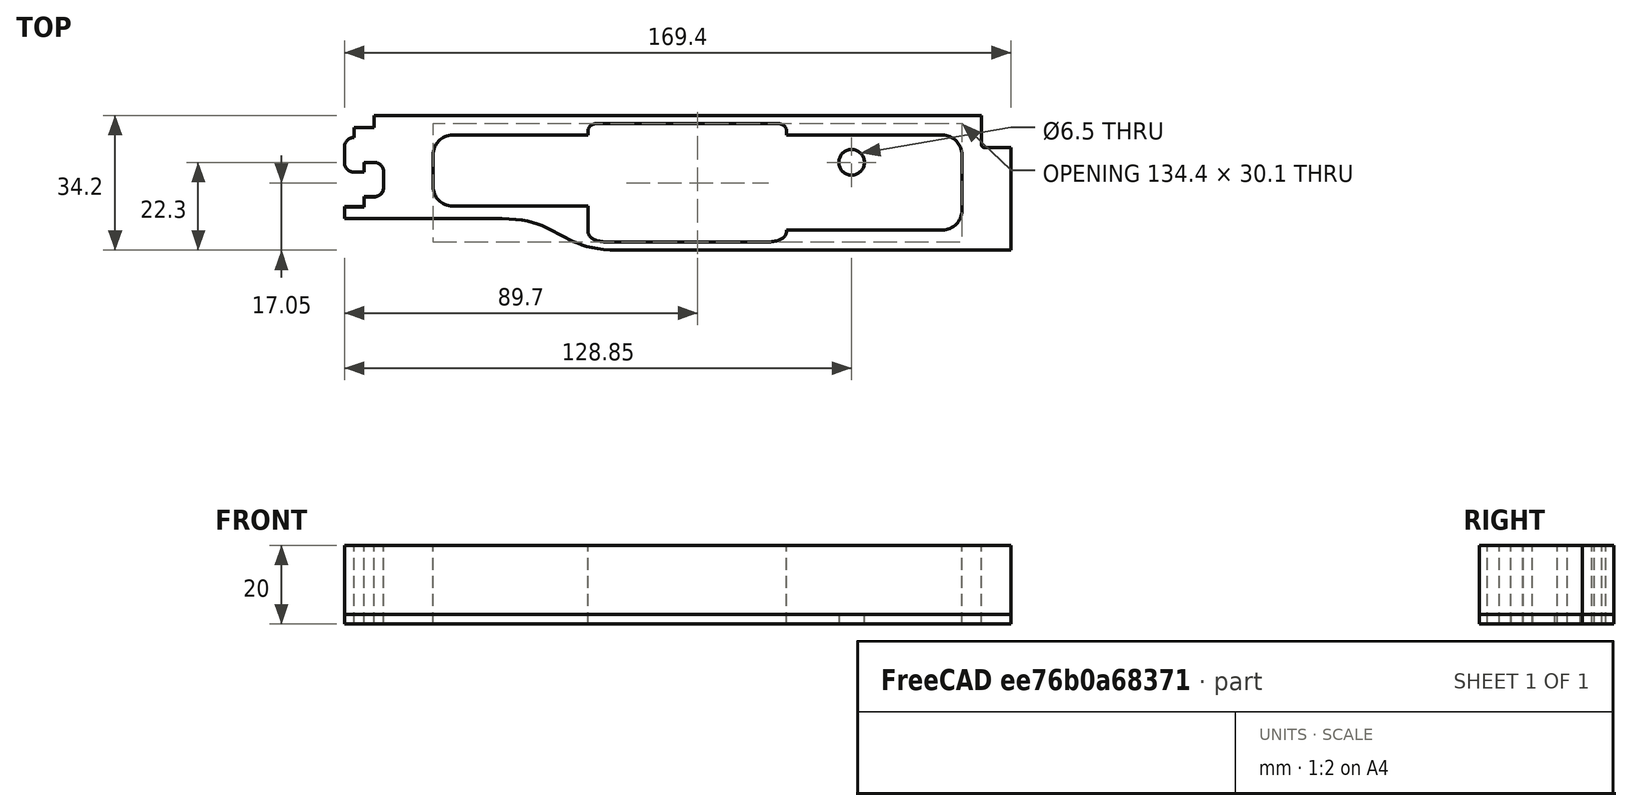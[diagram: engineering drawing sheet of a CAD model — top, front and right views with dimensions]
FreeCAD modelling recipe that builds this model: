
FCSTD DOCUMENT  (FreeCAD 0.19R0.19.2)
Label: v0_28
License: All rights reserved
LicenseURL: http://en.wikipedia.org/wiki/All_rights_reserved
objects: Sketcher::SketchObject×2, Part::Extrusion×2
note: 4 computed .brp shape members not serialized (recipe doc carries the construction recipe); baked Part::Feature solids carry a one-line shape summary decoded from their .brp

FEATURE [Sketcher::SketchObject] Sketch
  FullyConstrained = true
  sketch-geometry (33):
    g0: LineSegment StartX=0 StartY=0 StartZ=0 EndX=154.4 EndY=0 EndZ=0
    g1: Circle CenterX=121.35 CenterY=-11.9 CenterZ=0 NormalX=0 NormalY=0 NormalZ=1 AngleXU=0 Radius=3.25
    g2: LineSegment StartX=154.4 StartY=0 StartZ=0 EndX=154.4 EndY=-7.6 EndZ=0
    g3: ArcOfCircle CenterX=154.9 CenterY=-7.6 CenterZ=0 NormalX=0 NormalY=0 NormalZ=1 AngleXU=0 Radius=0.5 StartAngle=3.14159 EndAngle=4.71239
    g4: LineSegment StartX=-5 StartY=-3.1 StartZ=0 EndX=0 EndY=-3.1 EndZ=0
    g5: LineSegment StartX=-5 StartY=-3.1 StartZ=0 EndX=-5 EndY=-5.6 EndZ=0
    g6: LineSegment StartX=-7.5 StartY=-8.1 StartZ=0 EndX=-7.5 EndY=-11.85 EndZ=0
    g7: ArcOfCircle CenterX=-5 CenterY=-8.1 CenterZ=0 NormalX=0 NormalY=0 NormalZ=1 AngleXU=0 Radius=2.5 StartAngle=1.5708 EndAngle=3.14159
    g8: LineSegment StartX=-5 StartY=-14.35 StartZ=0 EndX=-2.5 EndY=-14.35 EndZ=0
    g9: ArcOfCircle CenterX=-5 CenterY=-11.85 CenterZ=0 NormalX=0 NormalY=0 NormalZ=1 AngleXU=0 Radius=2.5 StartAngle=3.14159 EndAngle=4.71239
    g10: LineSegment StartX=-2.5 StartY=-14.35 StartZ=0 EndX=-2.5 EndY=-11.85 EndZ=0
    g11: LineSegment StartX=-2.5 StartY=-11.85 StartZ=0 EndX=1.492e-13 EndY=-11.85 EndZ=0
    g12: ArcOfCircle CenterX=1.492e-13 CenterY=-14.35 CenterZ=0 NormalX=0 NormalY=0 NormalZ=1 AngleXU=0 Radius=2.5 StartAngle=8e-16 EndAngle=1.5708
    g13: LineSegment StartX=2.5 StartY=-14.35 StartZ=0 EndX=2.5 EndY=-18.1 EndZ=0
    g14: ArcOfCircle CenterX=1.474e-13 CenterY=-18.1 CenterZ=0 NormalX=0 NormalY=0 NormalZ=1 AngleXU=0 Radius=2.5 StartAngle=4.71239 EndAngle=6.28319
    g15: LineSegment StartX=-2.5 StartY=-20.6 StartZ=0 EndX=1.47e-13 EndY=-20.6 EndZ=0
    g16: LineSegment StartX=-2.5 StartY=-20.6 StartZ=0 EndX=-2.5 EndY=-23.1 EndZ=0
    g17: LineSegment StartX=-7.5 StartY=-23.1 StartZ=0 EndX=-2.5 EndY=-23.1 EndZ=0
    g18: LineSegment StartX=32.5209 StartY=-26.2 StartZ=0 EndX=-7.5 EndY=-26.2 EndZ=0
    g19: LineSegment StartX=61.85 StartY=-34.2 StartZ=0 EndX=161.9 EndY=-34.2 EndZ=0
    g20: LineSegment StartX=161.9 StartY=-8.1 StartZ=0 EndX=161.9 EndY=-34.2 EndZ=0
    g21: LineSegment StartX=154.9 StartY=-8.1 StartZ=0 EndX=161.9 EndY=-8.1 EndZ=0
    g22: LineSegment StartX=-7.5 StartY=-23.1 StartZ=0 EndX=-7.5 EndY=-26.2 EndZ=0
    g23: LineSegment StartX=0 StartY=0 StartZ=0 EndX=0 EndY=-3.1 EndZ=0
    g24-g28: Circle x5 (B-spline internal-alignment scaffolding for g29; pole/knot coordinates omitted)
    g29: BSplineCurve PolesCount=5 KnotsCount=3 Degree=3 IsPeriodic=0
    g30: GeomPoint X=61.85 Y=-34.2 Z=0
    g31: GeomPoint X=47.185 Y=-30.2 Z=0
    g32: GeomPoint X=32.5209 Y=-26.2 Z=0
  constraints (67):
    c: PointOnObject(g0,g-2)
    c: Horizontal(g0)
    c: Distance(g0) = 154.4
    c: DistanceY(g-1,g0) = 0
    c: Block(g1)
    c: Vertical(g2)
    c: Distance(g2) = 7.6
    c: Coincident(g2,g0)
    c: Block(g3)
    c: Horizontal(g4)
    c: Vertical(g5)
    c: Coincident(g5,g4)
    c: Vertical(g6)
    c: Coincident(g7,g5)
    c: Block(g7)
    c: Coincident(g6,g7)
    c: Horizontal(g8)
    c: Coincident(g9,g6)
    c: Block(g9)
    c: Block(g8)
    c: Vertical(g10)
    c: Coincident(g10,g8)
    c: Horizontal(g11)
    c: Coincident(g11,g10)
    c: Coincident(g12,g11)
    c: Vertical(g13)
    c: Block(g12)
    c: Coincident(g13,g12)
    c: Coincident(g14,g13)
    c: Block(g14)
    c: Horizontal(g15)
    c: Coincident(g15,g14)
    c: Vertical(g16)
    c: Coincident(g16,g15)
    c: Horizontal(g17)
    c: Coincident(g17,g16)
    c: Block(g16)
    c: Block(g4)
    c: Horizontal(g19)
    c: Horizontal(g18)
    c: Block(g18)
    c: Block(g19)
    c: Vertical(g20)
    c: Distance(g20) = 26.1
    c: Coincident(g20,g19)
    c: Horizontal(g21)
    c: Coincident(g21,g20)
    c: Coincident(g21,g3)
    c: Distance(g21) = 7
    c: Distance(g16) = 2.5
    c: Distance(g16) = 2.5
    c: Block(g17)
    c: Vertical(g22)
    c: Coincident(g22,g17)
    c: Coincident(g22,g18)
    c: Vertical(g23)
    c: Coincident(g23,g0)
    c: Coincident(g23,g4)
    c: Coincident(g29,g19)
    c: Weight(g24) = 1
    c: Equal(g24, g25-g28) x4
    c: Coincident(g29,g18)
    c: InternalAlignment(g24-g28 -> g29) x5
    c: InternalAlignment(g30,g29)
    c: InternalAlignment(g31,g29)
    c: InternalAlignment(g32,g29)
    c: Block(g29)
FEATURE [Part::Extrusion] Extrude
  Base = -> Sketch
  Dir = (0,0,1)
  DirMode = 2
  FaceMakerClass = Part::FaceMakerBullseye
  LengthFwd = 2.4
  LengthRev = 0
  Solid = true
  Symmetric = false
FEATURE [Sketcher::SketchObject] Sketch001
  FullyConstrained = true
  sketch-geometry (61):
    g0: ArcOfCircle CenterX=144.4 CenterY=-10 CenterZ=0 NormalX=0 NormalY=0 NormalZ=1 AngleXU=0 Radius=5 StartAngle=0 EndAngle=1.5708
    g1: ArcOfCircle CenterX=20 CenterY=-18 CenterZ=0 NormalX=0 NormalY=0 NormalZ=1 AngleXU=0 Radius=5 StartAngle=3.14159 EndAngle=4.71239
    g2: ArcOfCircle CenterX=20 CenterY=-10 CenterZ=0 NormalX=0 NormalY=0 NormalZ=1 AngleXU=0 Radius=5 StartAngle=1.5708 EndAngle=3.14159
    g3: LineSegment StartX=32.5209 StartY=-26.2 StartZ=0 EndX=-7.49911 EndY=-26.2 EndZ=0
    g4: LineSegment StartX=61.85 StartY=-34.2 StartZ=0 EndX=161.9 EndY=-34.2 EndZ=0
    g5: ArcOfCircle CenterX=144.4 CenterY=-24.1 CenterZ=0 NormalX=0 NormalY=0 NormalZ=1 AngleXU=0 Radius=5 StartAngle=4.71239 EndAngle=6.28319
    g6: Circle CenterX=104.85 CenterY=-29.2 CenterZ=0 NormalX=0 NormalY=0 NormalZ=1 AngleXU=0 Radius=1
    g7: Circle CenterX=104.85 CenterY=-32.2 CenterZ=0 NormalX=0 NormalY=0 NormalZ=1 AngleXU=0 Radius=1
    g8: Circle CenterX=98.85 CenterY=-32.2 CenterZ=0 NormalX=0 NormalY=0 NormalZ=1 AngleXU=0 Radius=1
    g9: BSplineCurve PolesCount=3 KnotsCount=2 Degree=2 IsPeriodic=0
    g10: GeomPoint X=104.85 Y=-29.2 Z=0
    g11: GeomPoint X=98.85 Y=-32.2 Z=0
    g12: Circle CenterX=54.35 CenterY=-29.2 CenterZ=0 NormalX=0 NormalY=0 NormalZ=1 AngleXU=0 Radius=1
    g13: Circle CenterX=60.35 CenterY=-32.2 CenterZ=0 NormalX=0 NormalY=0 NormalZ=1 AngleXU=0 Radius=1
    g14: BSplineCurve PolesCount=3 KnotsCount=2 Degree=2 IsPeriodic=0
    g15: GeomPoint X=54.35 Y=-29.2 Z=0
    g16: GeomPoint X=60.35 Y=-32.2 Z=0
    g17: ArcOfCircle CenterX=56.35 CenterY=-4.1 CenterZ=0 NormalX=0 NormalY=0 NormalZ=1 AngleXU=0 Radius=2 StartAngle=1.5708 EndAngle=3.14159
    g18: ArcOfCircle CenterX=102.85 CenterY=-4.1 CenterZ=0 NormalX=0 NormalY=0 NormalZ=1 AngleXU=0 Radius=2 StartAngle=1e-16 EndAngle=1.5708
    g19: LineSegment StartX=0 StartY=0 StartZ=0 EndX=154.4 EndY=0 EndZ=0
    g20: ArcOfCircle CenterX=154.9 CenterY=-7.6 CenterZ=0 NormalX=0 NormalY=0 NormalZ=1 AngleXU=0 Radius=0.5 StartAngle=3.14159 EndAngle=4.71239
    g21-g25: Circle x5 (B-spline internal-alignment scaffolding for g26; pole/knot coordinates omitted)
    g26: BSplineCurve PolesCount=5 KnotsCount=3 Degree=3 IsPeriodic=0
    g27: GeomPoint X=61.85 Y=-34.2 Z=0
    g28: GeomPoint X=47.1857 Y=-30.2 Z=0
    g29: GeomPoint X=32.5209 Y=-26.2 Z=0
    g30: LineSegment StartX=154.4 StartY=0 StartZ=0 EndX=154.4 EndY=-7.6 EndZ=0
    g31: LineSegment StartX=154.9 StartY=-8.1 StartZ=0 EndX=161.9 EndY=-8.1 EndZ=0
    g32: LineSegment StartX=161.9 StartY=-8.1 StartZ=0 EndX=161.9 EndY=-34.2 EndZ=0
    g33: LineSegment StartX=0 StartY=0 StartZ=0 EndX=0 EndY=-3.1 EndZ=0
    g34: LineSegment StartX=0 StartY=-3.1 StartZ=0 EndX=-5 EndY=-3.1 EndZ=0
    g35: LineSegment StartX=-5 StartY=-3.1 StartZ=0 EndX=-5 EndY=-5.6 EndZ=0
    g36: ArcOfCircle CenterX=-5 CenterY=-8.1 CenterZ=0 NormalX=0 NormalY=0 NormalZ=1 AngleXU=0 Radius=2.5 StartAngle=1.5708 EndAngle=3.14159
    g37: LineSegment StartX=-7.5 StartY=-8.1 StartZ=0 EndX=-7.5 EndY=-11.9 EndZ=0
    g38: ArcOfCircle CenterX=-5 CenterY=-11.9 CenterZ=0 NormalX=0 NormalY=0 NormalZ=1 AngleXU=0 Radius=2.5 StartAngle=3.14159 EndAngle=4.71239
    g39: LineSegment StartX=-5 StartY=-14.4 StartZ=0 EndX=-2.5 EndY=-14.4 EndZ=0
    g40: LineSegment StartX=-2.5 StartY=-14.4 StartZ=0 EndX=-2.5 EndY=-11.9 EndZ=0
    g41: LineSegment StartX=-2.5 StartY=-11.9 StartZ=0 EndX=2.833e-13 EndY=-11.9 EndZ=0
    g42: ArcOfCircle CenterX=2.833e-13 CenterY=-14.4 CenterZ=0 NormalX=0 NormalY=0 NormalZ=1 AngleXU=0 Radius=2.5 StartAngle=9e-16 EndAngle=1.5708
    g43: LineSegment StartX=2.5 StartY=-14.4 StartZ=0 EndX=2.5 EndY=-18.2 EndZ=0
    g44: ArcOfCircle CenterX=2.796e-13 CenterY=-18.2 CenterZ=0 NormalX=0 NormalY=0 NormalZ=1 AngleXU=0 Radius=2.5 StartAngle=4.71239 EndAngle=6.28319
    g45: LineSegment StartX=-2.5 StartY=-20.7 StartZ=0 EndX=8.16987e-07 EndY=-20.7 EndZ=0
    g46: LineSegment StartX=-2.5 StartY=-20.7 StartZ=0 EndX=-2.5 EndY=-23.2 EndZ=0
    g47: LineSegment StartX=-7.5 StartY=-23.2 StartZ=0 EndX=-2.5 EndY=-23.2 EndZ=0
    g48: LineSegment StartX=-7.5 StartY=-23.2 StartZ=0 EndX=-7.49911 EndY=-26.2 EndZ=0
    g49: LineSegment StartX=20 StartY=-5 StartZ=0 EndX=54.35 EndY=-5 EndZ=0
    g50: LineSegment StartX=54.35 StartY=-5 StartZ=0 EndX=54.35 EndY=-4.1 EndZ=0
    g51: LineSegment StartX=56.35 StartY=-2.1 StartZ=0 EndX=102.85 EndY=-2.1 EndZ=0
    g52: LineSegment StartX=104.85 StartY=-4.1 StartZ=0 EndX=104.85 EndY=-5 EndZ=0
    g53: LineSegment StartX=104.85 StartY=-5 StartZ=0 EndX=144.4 EndY=-5 EndZ=0
    g54: LineSegment StartX=149.4 StartY=-10 StartZ=0 EndX=149.4 EndY=-24.1 EndZ=0
    g55: LineSegment StartX=144.4 StartY=-29.1 StartZ=0 EndX=104.85 EndY=-29.1 EndZ=0
    g56: LineSegment StartX=104.85 StartY=-29.1 StartZ=0 EndX=104.85 EndY=-29.2 EndZ=0
    g57: LineSegment StartX=98.85 StartY=-32.2 StartZ=0 EndX=60.35 EndY=-32.2 EndZ=0
    g58: LineSegment StartX=54.35 StartY=-29.2 StartZ=0 EndX=54.35 EndY=-23 EndZ=0
    g59: LineSegment StartX=54.35 StartY=-23 StartZ=0 EndX=20 EndY=-23 EndZ=0
    g60: LineSegment StartX=15 StartY=-18 StartZ=0 EndX=15 EndY=-10 EndZ=0
  constraints (121):
    c: PointOnObject(g19,g-2)
    c: DistanceY(g-1,g19) = 0
    c: Block(g0)
    c: Block(g1)
    c: Block(g2)
    c: Horizontal(g4)
    c: Horizontal(g3)
    c: Block(g5)
    c: Distance(g3) = 40.02
    c: Weight(g6) = 1
    c: Equal(g6,g7)
    c: Equal(g6,g8)
    c: InternalAlignment(g6,g9)
    c: InternalAlignment(g7,g9)
    c: InternalAlignment(g8,g9)
    c: InternalAlignment(g10,g9)
    c: InternalAlignment(g11,g9)
    c: Block(g9)
    c: Weight(g12) = 1
    c: Equal(g12,g13)
    c: InternalAlignment(g12,g14)
    c: InternalAlignment(g13,g14)
    c: InternalAlignment(g15,g14)
    c: InternalAlignment(g16,g14)
    c: Block(g14)
    c: Block(g17)
    c: Block(g18)
    c: Horizontal(g19)
    c: Block(g4)
    c: Block(g19)
    c: Block(g20)
    c: Coincident(g26,g4)
    c: Weight(g21) = 1
    c: Equal(g21, g22-g25) x4
    c: Coincident(g26,g3)
    c: InternalAlignment(g21-g25 -> g26) x5
    c: InternalAlignment(g27,g26)
    c: InternalAlignment(g28,g26)
    c: InternalAlignment(g29,g26)
    c: Block(g26)
    c: Vertical(g30)
    c: Coincident(g30,g19)
    c: Coincident(g20,g30)
    c: Distance(g30) = 7.6
    c: Block(g30)
    c: Horizontal(g31)
    c: Coincident(g31,g20)
    c: Vertical(g32)
    c: Coincident(g32,g4)
    c: Coincident(g31,g32)
    c: Vertical(g33)
    c: Coincident(g33,g19)
    c: Distance(g33) = 3.1
    c: Coincident(g34,g33)
    c: Horizontal(g34)
    c: Distance(g34) = 5
    c: Vertical(g35)
    c: Distance(g35) = 2.5
    c: Coincident(g36,g35)
    c: Vertical(g37)
    c: Block(g36)
    c: Distance(g37) = 3.8
    c: Coincident(g38,g37)
    c: Block(g38)
    c: Horizontal(g39)
    c: Coincident(g39,g38)
    c: Distance(g39) = 2.5
    c: Vertical(g40)
    c: Coincident(g40,g39)
    c: Distance(g40) = 2.5
    c: Horizontal(g41)
    c: Distance(g41) = 2.5
    c: Coincident(g42,g41)
    c: Block(g42)
    c: Vertical(g43)
    c: Distance(g43) = 3.8
    c: Coincident(g44,g43)
    c: Block(g44)
    c: Horizontal(g45)
    c: Coincident(g45,g44)
    c: Distance(g45) = 2.5
    c: Vertical(g46)
    c: Coincident(g46,g45)
    c: Distance(g46) = 2.5
    c: Horizontal(g47)
    c: Coincident(g47,g46)
    c: Distance(g47) = 5
    c: Coincident(g48,g47)
    c: Coincident(g48,g3)
    c: Horizontal(g49)
    c: Coincident(g49,g2)
    c: Coincident(g50,g49)
    c: Coincident(g50,g17)
    c: Vertical(g50)
    c: Coincident(g51,g17)
    c: Coincident(g51,g18)
    c: Horizontal(g51)
    c: Coincident(g52,g18)
    c: Vertical(g52)
    c: Coincident(g53,g52)
    c: Coincident(g53,g0)
    c: Horizontal(g53)
    c: Coincident(g54,g0)
    c: Coincident(g54,g5)
    c: Vertical(g54)
    c: Coincident(g55,g5)
    c: Horizontal(g55)
    c: Coincident(g56,g55)
    c: Coincident(g56,g9)
    c: Vertical(g56)
    c: Coincident(g57,g9)
    c: Coincident(g57,g14)
    c: Horizontal(g57)
    c: Coincident(g58,g14)
    c: Vertical(g58)
    c: Coincident(g59,g58)
    c: Coincident(g59,g1)
    c: Horizontal(g59)
    c: Coincident(g60,g1)
    c: Coincident(g60,g2)
    c: Vertical(g60)
FEATURE [Part::Extrusion] Extrude001
  Base = -> Sketch001
  Dir = (0,0,1)
  DirMode = 2
  FaceMakerClass = Part::FaceMakerBullseye
  LengthFwd = 20
  LengthRev = 0
  Solid = true
  Symmetric = false
